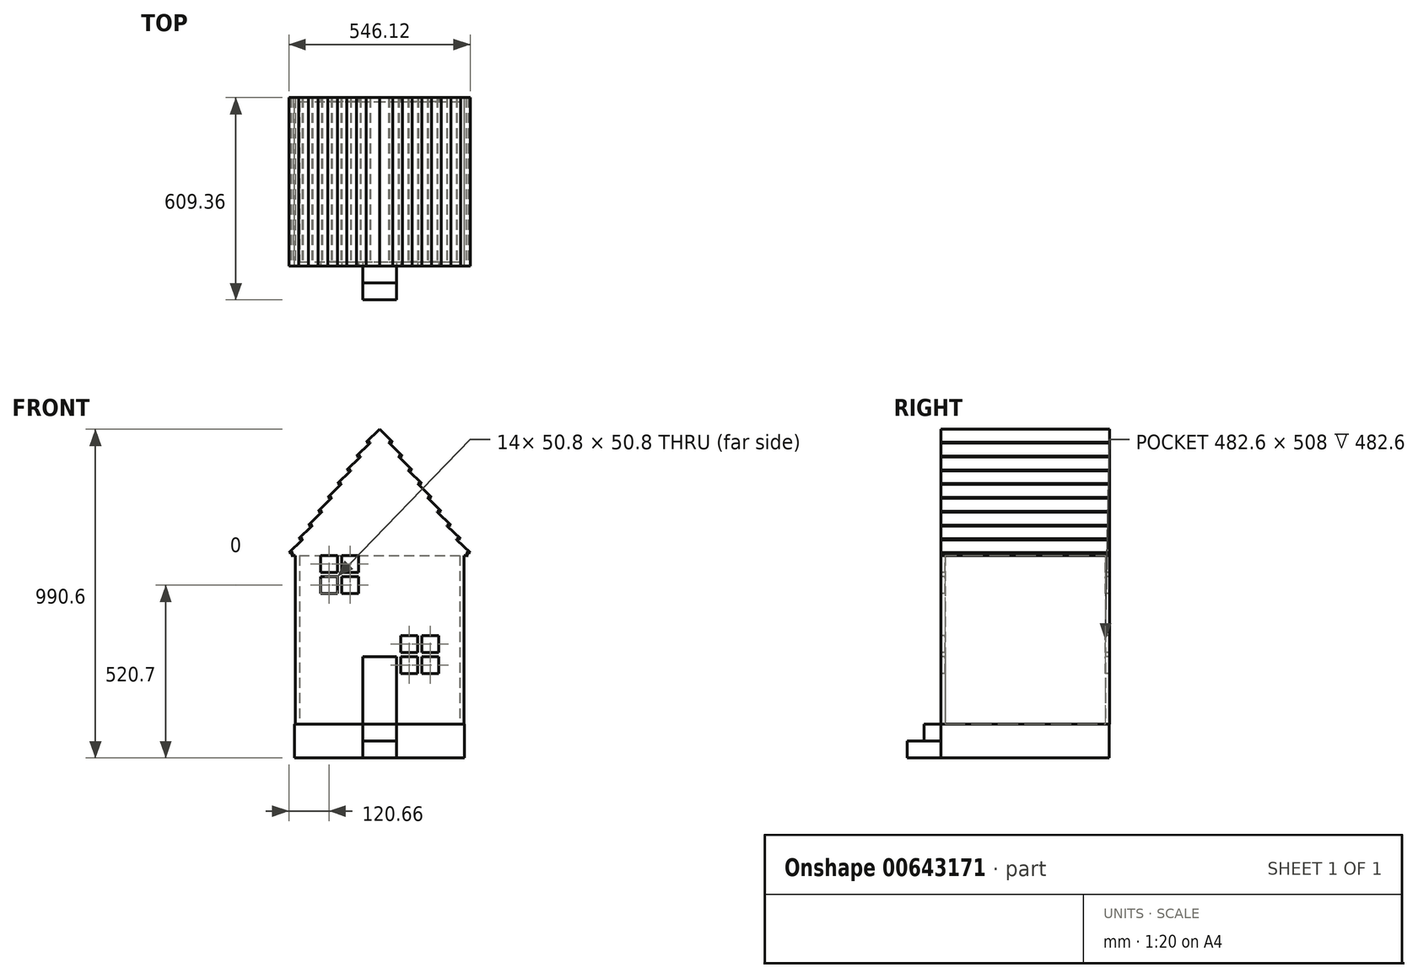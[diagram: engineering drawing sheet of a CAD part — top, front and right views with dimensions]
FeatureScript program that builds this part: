
annotation { "Feature Type Name" : "Feature", "Feature Type Description" : "" }
export const myFeature = defineFeature(function(context is Context, id is Id, definition is map)
    precondition{}
    {
        {
            var Q0;
            Q0=qCreatedBy(makeId("Top.planeOp"),FACE);
            var sketch = newSketch(context, id + "F0", { "sketchPlane" : qUnion([Q0])});
            skLineSegment(sketch, "E0.bottom", {"start": v(-254, 254) * mm, "end": v(254, 254) * mm});
            skLineSegment(sketch, "E0.top", {"start": v(-254, -254) * mm, "end": v(254, -254) * mm});
            skLineSegment(sketch, "E0.left", {"start": v(-254, 254) * mm, "end": v(-254, -254) * mm});
            skLineSegment(sketch, "E0.right", {"start": v(254, 254) * mm, "end": v(254, -254) * mm});
            skLineSegment(sketch, "E1.0", {"start": v(-241.3, 241.3) * mm, "end": v(241.3, 241.3) * mm});
            skLineSegment(sketch, "E1.1", {"start": v(-241.3, 241.3) * mm, "end": v(-241.3, -241.3) * mm});
            skLineSegment(sketch, "E1.2", {"start": v(-241.3, -241.3) * mm, "end": v(241.3, -241.3) * mm});
            skLineSegment(sketch, "E1.3", {"start": v(241.3, 241.3) * mm, "end": v(241.3, -241.3) * mm});
            skSolve(sketch);
        }
        {
            var Q0;
            Q0 = qSketchRegion(id + "F0", true);
            extrude(context, id + "F1", {"entities" : qUnion([Q0]), "depth" : 508 * mm, "offsetDistance" : 25.4 * mm});
        }
        {
            var Q0;
            Q0=makeQuery(id+"F1.opExtrude","SWEPT_FACE",FACE,{"disambiguationData":[OSD([sQuery(id+"F0.wireOp",EDGE,"E0.top")])]});
            var sketch = newSketch(context, id + "F2", { "sketchPlane" : qUnion([Q0])});
            skLineSegment(sketch, "E2", {"start": v(-266.7, 508) * mm, "end": v(266.7, 508) * mm});
            skLineSegment(sketch, "E3", {"start": v(0, 508) * mm, "end": v(0, 889) * mm, "construction": true});
            skPoint(sketch, "E3.endSnap0", {"position": v(0, 508) * mm});
            skLineSegment(sketch, "E4", {"start": v(-266.7, 508) * mm, "end": v(-260.36, 517.05) * mm, "construction": true});
            skLineSegment(sketch, "E5", {"start": v(266.7, 508) * mm, "end": v(0, 889) * mm, "construction": true});
            skLineSegment(sketch, "E6", {"start": v(0, 889) * mm, "end": v(-40, 849.99) * mm});
            skLineSegment(sketch, "E7", {"start": v(-40, 849.99) * mm, "end": v(-27.3, 849.99) * mm});
            skLineSegment(sketch, "E8.0.1.0", {"start": v(-29.13, 847.38) * mm, "end": v(-69.14, 808.37) * mm});
            skLineSegment(sketch, "E8.0.1.1", {"start": v(-69.14, 808.37) * mm, "end": v(-56.44, 808.37) * mm});
            skLineSegment(sketch, "E8.0.2.0", {"start": v(-58.26, 805.77) * mm, "end": v(-98.27, 766.75) * mm});
            skLineSegment(sketch, "E8.0.2.1", {"start": v(-98.27, 766.75) * mm, "end": v(-85.57, 766.75) * mm});
            skLineSegment(sketch, "E8.0.3.0", {"start": v(-87.4, 764.15) * mm, "end": v(-127.4, 725.14) * mm});
            skLineSegment(sketch, "E8.0.3.1", {"start": v(-127.4, 725.14) * mm, "end": v(-114.7, 725.14) * mm});
            skLineSegment(sketch, "E8.0.4.0", {"start": v(-116.53, 722.53) * mm, "end": v(-156.54, 683.52) * mm});
            skLineSegment(sketch, "E8.0.4.1", {"start": v(-156.54, 683.52) * mm, "end": v(-143.84, 683.52) * mm});
            skLineSegment(sketch, "E8.direction1", {"start": v(-40, 849.99) * mm, "end": v(-112.14, 849.99) * mm, "construction": true});
            skLineSegment(sketch, "E8.direction2", {"start": v(-40, 849.99) * mm, "end": v(-69.14, 808.37) * mm, "construction": true});
            skLineSegment(sketch, "E9.0.0.5", {"start": v(-145.66, 680.92) * mm, "end": v(-185.67, 641.9) * mm});
            skLineSegment(sketch, "E9.3.0.5", {"start": v(-185.67, 641.9) * mm, "end": v(-172.97, 641.9) * mm});
            skLineSegment(sketch, "E9.0.0.6", {"start": v(-174.8, 639.3) * mm, "end": v(-214.8, 600.29) * mm});
            skLineSegment(sketch, "E9.3.0.6", {"start": v(-214.8, 600.29) * mm, "end": v(-202.1, 600.29) * mm});
            skLineSegment(sketch, "E9.0.0.7", {"start": v(-203.92, 597.68) * mm, "end": v(-243.93, 558.67) * mm});
            skLineSegment(sketch, "E9.3.0.7", {"start": v(-243.93, 558.67) * mm, "end": v(-231.23, 558.67) * mm});
            skLineSegment(sketch, "E9.0.0.8", {"start": v(-233.06, 556.06) * mm, "end": v(-273.06, 517.05) * mm});
            skLineSegment(sketch, "E9.3.0.8", {"start": v(-273.06, 517.05) * mm, "end": v(-260.36, 517.05) * mm});
            skLineSegment(sketch, "E10", {"start": v(-27.3, 849.99) * mm, "end": v(-29.13, 847.38) * mm});
            skLineSegment(sketch, "E11.trimOffspring", {"start": v(-233.06, 556.06) * mm, "end": v(-231.23, 558.67) * mm, "construction": true});
            skLineSegment(sketch, "E12.trimOffspring", {"start": v(-260.36, 517.05) * mm, "end": v(-266.7, 508) * mm});
            skLineSegment(sketch, "E13.trimOffspring", {"start": v(-203.92, 597.68) * mm, "end": v(-202.1, 600.29) * mm, "construction": true});
            skLineSegment(sketch, "E14.trimOffspring", {"start": v(-231.23, 558.67) * mm, "end": v(-233.06, 556.06) * mm});
            skLineSegment(sketch, "E15.trimOffspring", {"start": v(-174.8, 639.3) * mm, "end": v(-172.97, 641.9) * mm, "construction": true});
            skLineSegment(sketch, "E16.trimOffspring", {"start": v(-202.1, 600.29) * mm, "end": v(-203.92, 597.68) * mm});
            skLineSegment(sketch, "E17.trimOffspring", {"start": v(-145.66, 680.92) * mm, "end": v(-143.84, 683.52) * mm, "construction": true});
            skLineSegment(sketch, "E18.trimOffspring", {"start": v(-172.97, 641.9) * mm, "end": v(-174.8, 639.3) * mm});
            skLineSegment(sketch, "E19.trimOffspring", {"start": v(-116.53, 722.53) * mm, "end": v(-114.7, 725.14) * mm, "construction": true});
            skLineSegment(sketch, "E20.trimOffspring", {"start": v(-143.84, 683.52) * mm, "end": v(-145.66, 680.92) * mm});
            skLineSegment(sketch, "E21.trimOffspring", {"start": v(-87.4, 764.15) * mm, "end": v(-85.57, 766.75) * mm, "construction": true});
            skLineSegment(sketch, "E22.trimOffspring", {"start": v(-114.7, 725.14) * mm, "end": v(-116.53, 722.53) * mm});
            skLineSegment(sketch, "E23.trimOffspring", {"start": v(-58.26, 805.77) * mm, "end": v(-56.44, 808.37) * mm, "construction": true});
            skLineSegment(sketch, "E24.trimOffspring", {"start": v(-85.57, 766.75) * mm, "end": v(-87.4, 764.15) * mm});
            skLineSegment(sketch, "E25.trimOffspring", {"start": v(-29.13, 847.38) * mm, "end": v(-27.3, 849.99) * mm, "construction": true});
            skLineSegment(sketch, "E26.trimOffspring", {"start": v(-56.44, 808.37) * mm, "end": v(-58.26, 805.77) * mm});
            skLineSegment(sketch, "E27.MirrorCS", {"start": v(266.7, 508) * mm, "end": v(260.36, 517.05) * mm, "construction": true});
            skLineSegment(sketch, "E28.MirrorCS", {"start": v(273.06, 517.05) * mm, "end": v(260.36, 517.05) * mm});
            skLineSegment(sketch, "E29.MirrorCS", {"start": v(233.06, 556.06) * mm, "end": v(273.06, 517.05) * mm});
            skLineSegment(sketch, "E30.MirrorCS", {"start": v(233.06, 556.06) * mm, "end": v(231.23, 558.67) * mm, "construction": true});
            skLineSegment(sketch, "E31.MirrorCS", {"start": v(243.93, 558.67) * mm, "end": v(231.23, 558.67) * mm});
            skLineSegment(sketch, "E32.MirrorCS", {"start": v(203.92, 597.68) * mm, "end": v(243.93, 558.67) * mm});
            skLineSegment(sketch, "E33.MirrorCS", {"start": v(203.92, 597.68) * mm, "end": v(202.1, 600.29) * mm, "construction": true});
            skLineSegment(sketch, "E34.MirrorCS", {"start": v(214.8, 600.29) * mm, "end": v(202.1, 600.29) * mm});
            skLineSegment(sketch, "E35.MirrorCS", {"start": v(174.8, 639.3) * mm, "end": v(214.8, 600.29) * mm});
            skLineSegment(sketch, "E36.MirrorCS", {"start": v(174.8, 639.3) * mm, "end": v(172.97, 641.9) * mm, "construction": true});
            skLineSegment(sketch, "E37.MirrorCS", {"start": v(185.67, 641.9) * mm, "end": v(172.97, 641.9) * mm});
            skLineSegment(sketch, "E38.MirrorCS", {"start": v(145.66, 680.92) * mm, "end": v(185.67, 641.9) * mm});
            skLineSegment(sketch, "E39.MirrorCS", {"start": v(145.66, 680.92) * mm, "end": v(143.84, 683.52) * mm, "construction": true});
            skLineSegment(sketch, "E40.MirrorCS", {"start": v(156.54, 683.52) * mm, "end": v(143.84, 683.52) * mm});
            skLineSegment(sketch, "E41.MirrorCS", {"start": v(116.53, 722.53) * mm, "end": v(156.54, 683.52) * mm});
            skLineSegment(sketch, "E42.MirrorCS", {"start": v(116.53, 722.53) * mm, "end": v(114.7, 725.14) * mm, "construction": true});
            skLineSegment(sketch, "E43.MirrorCS", {"start": v(127.4, 725.14) * mm, "end": v(114.7, 725.14) * mm});
            skLineSegment(sketch, "E44.MirrorCS", {"start": v(87.4, 764.15) * mm, "end": v(127.4, 725.14) * mm});
            skLineSegment(sketch, "E45.MirrorCS", {"start": v(87.4, 764.15) * mm, "end": v(85.57, 766.75) * mm, "construction": true});
            skLineSegment(sketch, "E46.MirrorCS", {"start": v(98.27, 766.75) * mm, "end": v(85.57, 766.75) * mm});
            skLineSegment(sketch, "E47.MirrorCS", {"start": v(58.26, 805.77) * mm, "end": v(98.27, 766.75) * mm});
            skLineSegment(sketch, "E48.MirrorCS", {"start": v(58.26, 805.77) * mm, "end": v(56.44, 808.37) * mm, "construction": true});
            skLineSegment(sketch, "E49.MirrorCS", {"start": v(69.14, 808.37) * mm, "end": v(56.44, 808.37) * mm});
            skLineSegment(sketch, "E50.MirrorCS", {"start": v(29.13, 847.38) * mm, "end": v(69.14, 808.37) * mm});
            skLineSegment(sketch, "E51.MirrorCS", {"start": v(29.13, 847.38) * mm, "end": v(27.3, 849.99) * mm, "construction": true});
            skLineSegment(sketch, "E52.MirrorCS", {"start": v(40, 849.99) * mm, "end": v(27.3, 849.99) * mm});
            skLineSegment(sketch, "E53.MirrorCS", {"start": v(0, 889) * mm, "end": v(40, 849.99) * mm});
            skLineSegment(sketch, "E54", {"start": v(27.3, 849.99) * mm, "end": v(29.13, 847.38) * mm});
            skLineSegment(sketch, "E55", {"start": v(56.44, 808.37) * mm, "end": v(58.26, 805.77) * mm});
            skLineSegment(sketch, "E56", {"start": v(85.57, 766.75) * mm, "end": v(87.4, 764.15) * mm});
            skLineSegment(sketch, "E57", {"start": v(114.7, 725.14) * mm, "end": v(116.53, 722.53) * mm});
            skLineSegment(sketch, "E58", {"start": v(143.84, 683.52) * mm, "end": v(145.66, 680.92) * mm});
            skLineSegment(sketch, "E59", {"start": v(174.8, 639.3) * mm, "end": v(172.97, 641.9) * mm});
            skLineSegment(sketch, "E60", {"start": v(203.92, 597.68) * mm, "end": v(202.1, 600.29) * mm});
            skLineSegment(sketch, "E61", {"start": v(231.23, 558.67) * mm, "end": v(233.06, 556.06) * mm});
            skLineSegment(sketch, "E62", {"start": v(260.36, 517.05) * mm, "end": v(266.7, 508) * mm});
            skSolve(sketch);
        }
        {
            var Q0;
            Q0 = qSketchRegion(id + "F2", true);
            extrude(context, id + "F3", {"entities" : qUnion([Q0]), "operationType" : NewBodyOperationType.ADD, "oppositeDirection" : true, "depth" : 508 * mm, "offsetDistance" : 25.4 * mm});
        }
        {
            var Q0;
            Q0=makeQuery(id+"F3.boolean.opBoolean","MERGE",FACE,{"derivedFrom":[makeQuery(id+"F1.opExtrude","SWEPT_FACE",FACE,{"disambiguationData":[OSD([sQuery(id+"F0.wireOp",EDGE,"E0.top")])]}),makeQuery(id+"F3.opExtrude","CAP_FACE",FACE,{"disambiguationData":[OSD([sQuery(id+"F2.wireOp",EDGE,"E2"),sQuery(id+"F2.wireOp",EDGE,"E6"),sQuery(id+"F2.wireOp",EDGE,"E7"),sQuery(id+"F2.wireOp",EDGE,"E8.0.1.0"),sQuery(id+"F2.wireOp",EDGE,"E8.0.1.1"),sQuery(id+"F2.wireOp",EDGE,"E8.0.2.0"),sQuery(id+"F2.wireOp",EDGE,"E8.0.2.1"),sQuery(id+"F2.wireOp",EDGE,"E8.0.3.0"),sQuery(id+"F2.wireOp",EDGE,"E8.0.3.1"),sQuery(id+"F2.wireOp",EDGE,"E8.0.4.0"),sQuery(id+"F2.wireOp",EDGE,"E8.0.4.1"),sQuery(id+"F2.wireOp",EDGE,"E9.0.0.5"),sQuery(id+"F2.wireOp",EDGE,"E9.3.0.5"),sQuery(id+"F2.wireOp",EDGE,"E9.0.0.6"),sQuery(id+"F2.wireOp",EDGE,"E9.3.0.6"),sQuery(id+"F2.wireOp",EDGE,"E9.0.0.7"),sQuery(id+"F2.wireOp",EDGE,"E9.3.0.7"),sQuery(id+"F2.wireOp",EDGE,"E9.0.0.8"),sQuery(id+"F2.wireOp",EDGE,"E9.3.0.8"),sQuery(id+"F2.wireOp",EDGE,"E10"),sQuery(id+"F2.wireOp",EDGE,"E12.trimOffspring"),sQuery(id+"F2.wireOp",EDGE,"E14.trimOffspring"),sQuery(id+"F2.wireOp",EDGE,"E16.trimOffspring"),sQuery(id+"F2.wireOp",EDGE,"E18.trimOffspring"),sQuery(id+"F2.wireOp",EDGE,"E20.trimOffspring"),sQuery(id+"F2.wireOp",EDGE,"E22.trimOffspring"),sQuery(id+"F2.wireOp",EDGE,"E24.trimOffspring"),sQuery(id+"F2.wireOp",EDGE,"E26.trimOffspring"),sQuery(id+"F2.wireOp",EDGE,"E28.MirrorCS"),sQuery(id+"F2.wireOp",EDGE,"E29.MirrorCS"),sQuery(id+"F2.wireOp",EDGE,"E31.MirrorCS"),sQuery(id+"F2.wireOp",EDGE,"E32.MirrorCS"),sQuery(id+"F2.wireOp",EDGE,"E34.MirrorCS"),sQuery(id+"F2.wireOp",EDGE,"E35.MirrorCS"),sQuery(id+"F2.wireOp",EDGE,"E37.MirrorCS"),sQuery(id+"F2.wireOp",EDGE,"E38.MirrorCS"),sQuery(id+"F2.wireOp",EDGE,"E40.MirrorCS"),sQuery(id+"F2.wireOp",EDGE,"E41.MirrorCS"),sQuery(id+"F2.wireOp",EDGE,"E43.MirrorCS"),sQuery(id+"F2.wireOp",EDGE,"E44.MirrorCS"),sQuery(id+"F2.wireOp",EDGE,"E46.MirrorCS"),sQuery(id+"F2.wireOp",EDGE,"E47.MirrorCS"),sQuery(id+"F2.wireOp",EDGE,"E49.MirrorCS"),sQuery(id+"F2.wireOp",EDGE,"E50.MirrorCS"),sQuery(id+"F2.wireOp",EDGE,"E52.MirrorCS"),sQuery(id+"F2.wireOp",EDGE,"E53.MirrorCS"),sQuery(id+"F2.wireOp",EDGE,"E54"),sQuery(id+"F2.wireOp",EDGE,"E55"),sQuery(id+"F2.wireOp",EDGE,"E56"),sQuery(id+"F2.wireOp",EDGE,"E57"),sQuery(id+"F2.wireOp",EDGE,"E58"),sQuery(id+"F2.wireOp",EDGE,"E59"),sQuery(id+"F2.wireOp",EDGE,"E60"),sQuery(id+"F2.wireOp",EDGE,"E61"),sQuery(id+"F2.wireOp",EDGE,"E62")])],"isStart":true})]});
            var sketch = newSketch(context, id + "F4", { "sketchPlane" : qUnion([Q0])});
            skLineSegment(sketch, "E63", {"start": v(0, 0) * mm, "end": v(0, 699.68) * mm, "construction": true});
            skPoint(sketch, "E63.endSnap0", {"position": v(0, 0) * mm});
            skLineSegment(sketch, "E64.bottom", {"start": v(25.4, 254) * mm, "end": v(228.6, 254) * mm, "construction": true});
            skLineSegment(sketch, "E64.top", {"start": v(25.4, 50.8) * mm, "end": v(228.6, 50.8) * mm, "construction": true});
            skLineSegment(sketch, "E64.left", {"start": v(25.4, 254) * mm, "end": v(25.4, 50.8) * mm, "construction": true});
            skLineSegment(sketch, "E64.right", {"start": v(228.6, 254) * mm, "end": v(228.6, 50.8) * mm, "construction": true});
            skLineSegment(sketch, "E65.bottom", {"start": v(-63.5, 508) * mm, "end": v(-114.3, 508) * mm});
            skLineSegment(sketch, "E65.top", {"start": v(-63.5, 457.2) * mm, "end": v(-114.3, 457.2) * mm});
            skLineSegment(sketch, "E65.left", {"start": v(-63.5, 508) * mm, "end": v(-63.5, 457.2) * mm});
            skLineSegment(sketch, "E65.right", {"start": v(-114.3, 508) * mm, "end": v(-114.3, 457.2) * mm});
            skLineSegment(sketch, "E66.bottom", {"start": v(-177.8, 444.5) * mm, "end": v(-127, 444.5) * mm});
            skLineSegment(sketch, "E66.top", {"start": v(-177.8, 393.7) * mm, "end": v(-127, 393.7) * mm});
            skLineSegment(sketch, "E66.left", {"start": v(-177.8, 444.5) * mm, "end": v(-177.8, 393.7) * mm});
            skLineSegment(sketch, "E66.right", {"start": v(-127, 444.5) * mm, "end": v(-127, 393.7) * mm});
            skLineSegment(sketch, "E67.bottom", {"start": v(-114.3, 444.5) * mm, "end": v(-63.5, 444.5) * mm});
            skLineSegment(sketch, "E67.top", {"start": v(-114.3, 393.7) * mm, "end": v(-63.5, 393.7) * mm});
            skLineSegment(sketch, "E67.left", {"start": v(-114.3, 444.5) * mm, "end": v(-114.3, 393.7) * mm});
            skLineSegment(sketch, "E67.right", {"start": v(-63.5, 444.5) * mm, "end": v(-63.5, 393.7) * mm});
            skLineSegment(sketch, "E68", {"start": v(-254, 393.7) * mm, "end": v(0, 393.7) * mm, "construction": true});
            skLineSegment(sketch, "E69.bottom", {"start": v(-177.8, 508) * mm, "end": v(-127, 508) * mm});
            skLineSegment(sketch, "E69.top", {"start": v(-177.8, 457.2) * mm, "end": v(-127, 457.2) * mm});
            skLineSegment(sketch, "E69.left", {"start": v(-177.8, 508) * mm, "end": v(-177.8, 457.2) * mm});
            skLineSegment(sketch, "E69.right", {"start": v(-127, 508) * mm, "end": v(-127, 457.2) * mm});
            skLineSegment(sketch, "E70.bottom", {"start": v(177.8, 266.7) * mm, "end": v(127, 266.7) * mm});
            skLineSegment(sketch, "E70.top", {"start": v(177.8, 215.9) * mm, "end": v(127, 215.9) * mm});
            skLineSegment(sketch, "E70.left", {"start": v(177.8, 266.7) * mm, "end": v(177.8, 215.9) * mm});
            skLineSegment(sketch, "E70.right", {"start": v(127, 266.7) * mm, "end": v(127, 215.9) * mm});
            skLineSegment(sketch, "E71.bottom", {"start": v(63.5, 203.2) * mm, "end": v(114.3, 203.2) * mm});
            skLineSegment(sketch, "E71.top", {"start": v(63.5, 152.4) * mm, "end": v(114.3, 152.4) * mm});
            skLineSegment(sketch, "E71.left", {"start": v(63.5, 203.2) * mm, "end": v(63.5, 152.4) * mm});
            skLineSegment(sketch, "E71.right", {"start": v(114.3, 203.2) * mm, "end": v(114.3, 152.4) * mm});
            skLineSegment(sketch, "E72.bottom", {"start": v(127, 203.2) * mm, "end": v(177.8, 203.2) * mm});
            skLineSegment(sketch, "E72.top", {"start": v(127, 152.4) * mm, "end": v(177.8, 152.4) * mm});
            skLineSegment(sketch, "E72.left", {"start": v(127, 203.2) * mm, "end": v(127, 152.4) * mm});
            skLineSegment(sketch, "E72.right", {"start": v(177.8, 203.2) * mm, "end": v(177.8, 152.4) * mm});
            skLineSegment(sketch, "E73.bottom", {"start": v(63.5, 266.7) * mm, "end": v(114.3, 266.7) * mm});
            skLineSegment(sketch, "E73.top", {"start": v(63.5, 215.9) * mm, "end": v(114.3, 215.9) * mm});
            skLineSegment(sketch, "E73.left", {"start": v(63.5, 266.7) * mm, "end": v(63.5, 215.9) * mm});
            skLineSegment(sketch, "E73.right", {"start": v(114.3, 266.7) * mm, "end": v(114.3, 215.9) * mm});
            skSolve(sketch);
        }
        {
            var Q0;
            Q0 = qSketchRegion(id + "F4", true);
            extrude(context, id + "F5", {"entities" : qUnion([Q0]), "operationType" : NewBodyOperationType.REMOVE, "oppositeDirection" : true, "depth" : 734.06 * mm, "offsetDistance" : 25.4 * mm});
        }
        {
            var Q0;
            Q0=makeQuery(id+"F4.imprint","IMPRINT",FACE,{"disambiguationData":[TD([[makeQuery(id+"F4.imprint","IMPRINT",EDGE,{"derivedFrom":sQuery(id+"F4.wireOp",EDGE,"E65.bottom")}),-1.0]])]});
            var sketch = newSketch(context, id + "F6", { "sketchPlane" : qUnion([Q0])});
            skLineSegment(sketch, "E74.bottom", {"start": v(50.8, 0) * mm, "end": v(-50.8, 0) * mm});
            skLineSegment(sketch, "E74.top", {"start": v(50.8, 203.2) * mm, "end": v(-50.8, 203.2) * mm});
            skLineSegment(sketch, "E74.left", {"start": v(50.8, 0) * mm, "end": v(50.8, 203.2) * mm});
            skLineSegment(sketch, "E74.right", {"start": v(-50.8, 0) * mm, "end": v(-50.8, 203.2) * mm});
            skSolve(sketch);
        }
        {
            var Q0;
            Q0 = qSketchRegion(id + "F6", true);
            extrude(context, id + "F7", {"entities" : qUnion([Q0]), "operationType" : NewBodyOperationType.REMOVE, "oppositeDirection" : true, "depth" : 25.4 * mm, "offsetDistance" : 25.4 * mm});
        }
        {
            var Q0;
            Q0=qCreatedBy(makeId("Top.planeOp"),FACE);
            var sketch = newSketch(context, id + "F8", { "sketchPlane" : qUnion([Q0])});
            skCircle(sketch, "E75", {"center": v(-126.47, 89.43) * mm, "radius": 64.51 * mm});
            skCircle(sketch, "E76", {"center": v(-126.47, 89.43) * mm, "radius": 51.51 * mm});
            skSolve(sketch);
        }
        {
            var Q0;
            Q0=sQuery(id+"F8.wireOp",EDGE,"E76");
            var Q1;
            Q1=sQuery(id+"F8.wireOp",EDGE,"E75");
            extrude(context, id + "F9", {"bodyType" : ToolBodyType.SURFACE, "surfaceEntities" : qUnion([Q0, Q1]), "depth" : 1125.22 * mm, "offsetDistance" : 25.4 * mm});
        }
        {
            var Q0;
            Q0=qCreatedBy(makeId("Top.planeOp"),FACE);
            var sketch = newSketch(context, id + "F10", { "sketchPlane" : qUnion([Q0])});
            skLineSegment(sketch, "E77.bottom", {"start": v(254.97, -253.76) * mm, "end": v(-256.27, -253.76) * mm});
            skLineSegment(sketch, "E77.top", {"start": v(254.97, 252.82) * mm, "end": v(-256.27, 252.82) * mm});
            skLineSegment(sketch, "E77.left", {"start": v(254.97, -253.76) * mm, "end": v(254.97, 252.82) * mm});
            skLineSegment(sketch, "E77.right", {"start": v(-256.27, -253.76) * mm, "end": v(-256.27, 252.82) * mm});
            skSolve(sketch);
        }
        {
            var Q0;
            Q0 = qSketchRegion(id + "F10", true);
            extrude(context, id + "F11", {"entities" : qUnion([Q0]), "operationType" : NewBodyOperationType.ADD, "oppositeDirection" : true, "depth" : 101.6 * mm, "offsetDistance" : 25.4 * mm});
        }
        {
            var Q0;
            Q0=makeQuery(id+"F11.opExtrude","SWEPT_FACE",FACE,{"disambiguationData":[OSD([sQuery(id+"F10.wireOp",EDGE,"E77.bottom")])]});
            var sketch = newSketch(context, id + "F12", { "sketchPlane" : qUnion([Q0])});
            skLineSegment(sketch, "E78.bottom", {"start": v(-50.8, -101.6) * mm, "end": v(50.8, -101.6) * mm});
            skLineSegment(sketch, "E78.top", {"start": v(-50.8, -50.8) * mm, "end": v(50.8, -50.8) * mm});
            skLineSegment(sketch, "E78.left", {"start": v(-50.8, -101.6) * mm, "end": v(-50.8, -50.8) * mm});
            skLineSegment(sketch, "E78.right", {"start": v(50.8, -101.6) * mm, "end": v(50.8, -50.8) * mm});
            skSolve(sketch);
        }
        {
            var Q0;
            Q0 = qSketchRegion(id + "F12", true);
            extrude(context, id + "F13", {"entities" : qUnion([Q0]), "operationType" : NewBodyOperationType.ADD, "depth" : 101.6 * mm, "offsetDistance" : 25.4 * mm});
        }
        {
            var Q0;
            Q0=makeQuery(id+"F11.opExtrude","SWEPT_FACE",FACE,{"disambiguationData":[OSD([sQuery(id+"F10.wireOp",EDGE,"E77.bottom")])]});
            var sketch = newSketch(context, id + "F14", { "sketchPlane" : qUnion([Q0])});
            skLineSegment(sketch, "E79.bottom", {"start": v(50.8, -50.8) * mm, "end": v(-50.8, -50.8) * mm});
            skLineSegment(sketch, "E79.top", {"start": v(50.8, 0) * mm, "end": v(-50.8, 0) * mm});
            skLineSegment(sketch, "E79.left", {"start": v(50.8, -50.8) * mm, "end": v(50.8, 0) * mm});
            skLineSegment(sketch, "E79.right", {"start": v(-50.8, -50.8) * mm, "end": v(-50.8, 0) * mm});
            skSolve(sketch);
        }
        {
            var Q0;
            Q0 = qSketchRegion(id + "F14", true);
            extrude(context, id + "F15", {"entities" : qUnion([Q0]), "depth" : 50.8 * mm, "offsetDistance" : 25.4 * mm});
        }
    });
